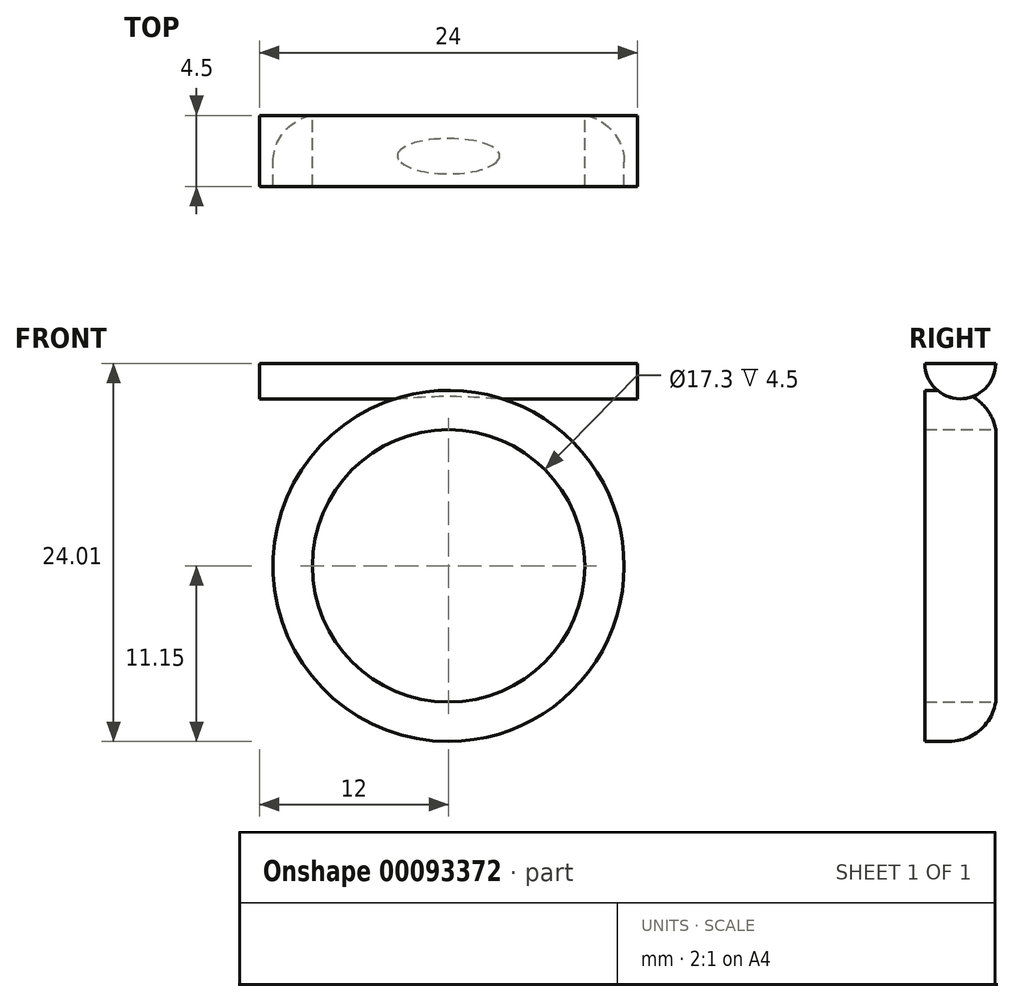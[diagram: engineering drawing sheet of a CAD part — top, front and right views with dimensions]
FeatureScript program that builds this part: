
annotation { "Feature Type Name" : "Feature", "Feature Type Description" : "" }
export const myFeature = defineFeature(function(context is Context, id is Id, definition is map)
    precondition{}
    {
        {
            var Q0;
            Q0=qCreatedBy(makeId("Front.planeOp"),FACE);
            var sketch = newSketch(context, id + "F0", { "sketchPlane" : qUnion([Q0])});
            skCircle(sketch, "E0", {"center": v(0, 0) * mm, "radius": 8.65 * mm});
            skCircle(sketch, "E1.0", {"center": v(0, 0) * mm, "radius": 11.15 * mm});
            skPoint(sketch, "E2", {"position": v(0, 11.15) * mm});
            skPoint(sketch, "E3", {"position": v(11.15, 0) * mm});
            skPoint(sketch, "E4", {"position": v(-11.15, 0) * mm});
            skLineSegment(sketch, "E5", {"start": v(11.15, 0) * mm, "end": v(11.15, 11.15) * mm});
            skLineSegment(sketch, "E6", {"start": v(11.15, 11.15) * mm, "end": v(0, 11.15) * mm});
            skLineSegment(sketch, "E7.MirrorCS", {"start": v(-11.15, 0) * mm, "end": v(-11.15, 11.15) * mm});
            skPoint(sketch, "E8", {"position": v(-4, 11.15) * mm});
            skPoint(sketch, "E9", {"position": v(-9.15, 11.15) * mm});
            skLineSegment(sketch, "E10", {"start": v(-11.15, 11.15) * mm, "end": v(0, 11.15) * mm});
            skSolve(sketch);
        }
        {
            var Q0;
            Q0=makeQuery(id+"F0.imprint","IMPRINT",FACE,{"disambiguationData":[TD([[makeQuery(id+"F0.imprint","IMPRINT",EDGE,{"derivedFrom":sQuery(id+"F0.wireOp",EDGE,"E0")}),-1.0]])]});
            var Q1;
            {var subQ0=sQuery(id+"F0.wireOp",EDGE,"00bf0574-2f39-41c0-8409-fd84e967d9b20.MirrorCS");Q1=makeQuery(id+"F0.imprint","IMPRINT",FACE,{"disambiguationData":[TD([[makeQuery(id+"F0.imprint","IMPRINT",EDGE,{"derivedFrom":subQ0}),-1.0]])]});}
            var Q2;
            Q2=makeQuery(id+"F0.imprint","IMPRINT",FACE,{"disambiguationData":[TD([[makeQuery(id+"F0.imprint","IMPRINT",EDGE,{"derivedFrom":sQuery(id+"F0.wireOp",EDGE,"IftZQGqq-PVLr-zGN3-dlVx-n0IfTxKKuJgI")}),-1.0]])]});
            extrude(context, id + "F1", {"entities" : qUnion([Q0, Q1, Q2]), "depth" : 2.25 * mm, "hasSecondDirection" : true, "secondDirectionOppositeDirection" : true, "secondDirectionDepth" : 2.25 * mm});
        }
        {
            var Q0;
            Q0=qCreatedBy(makeId("Right.planeOp"),FACE);
            var sketch = newSketch(context, id + "F2", { "sketchPlane" : qUnion([Q0])});
            skPoint(sketch, "E11", {"position": v(0, 10.61) * mm});
            skLineSegment(sketch, "E12", {"start": v(0, 10.61) * mm, "end": v(0, 12.86) * mm, "construction": true});
            skCircle(sketch, "E13", {"center": v(0, 12.86) * mm, "radius": 2.25 * mm});
            skLineSegment(sketch, "E14", {"start": v(0, 12.86) * mm, "end": v(2.25, 12.86) * mm});
            skLineSegment(sketch, "E15", {"start": v(2.25, 12.86) * mm, "end": v(-2.25, 12.86) * mm});
            skSolve(sketch);
        }
        {
            var Q0;
            {var subQ0=sQuery(id+"F2.wireOp",EDGE,"E15");var subQ4=makeQuery(id+"F2.imprint","IMPRINT",VERTEX,{"derivedFrom":subQ0});Q0=makeQuery(id+"F2.imprint","IMPRINT",FACE,{"disambiguationData":[TD([[makeQuery(id+"F2.imprint","IMPRINT",EDGE,{"disambiguationData":[TD([[subQ4,1.0]])],"derivedFrom":subQ0}),1.0]])]});}
            extrude(context, id + "F3", {"entities" : qUnion([Q0]), "operationType" : NewBodyOperationType.ADD, "depth" : 12 * mm, "hasSecondDirection" : true, "secondDirectionOppositeDirection" : true, "secondDirectionDepth" : 12 * mm});
        }
        {
            var Q0;
            Q0=makeQuery(id+"F1.opExtrude","CAP_EDGE",EDGE,{"disambiguationData":[OSD([sQuery(id+"F0.wireOp",EDGE,"E1.0")])],"isStart":true});
            fillet(context, id + "F4", {"entities" : qUnion([Q0]), "radius" : 3 * mm, "tangentPropagation" : true, "allowEdgeOverflow" : false});
        }
    });
